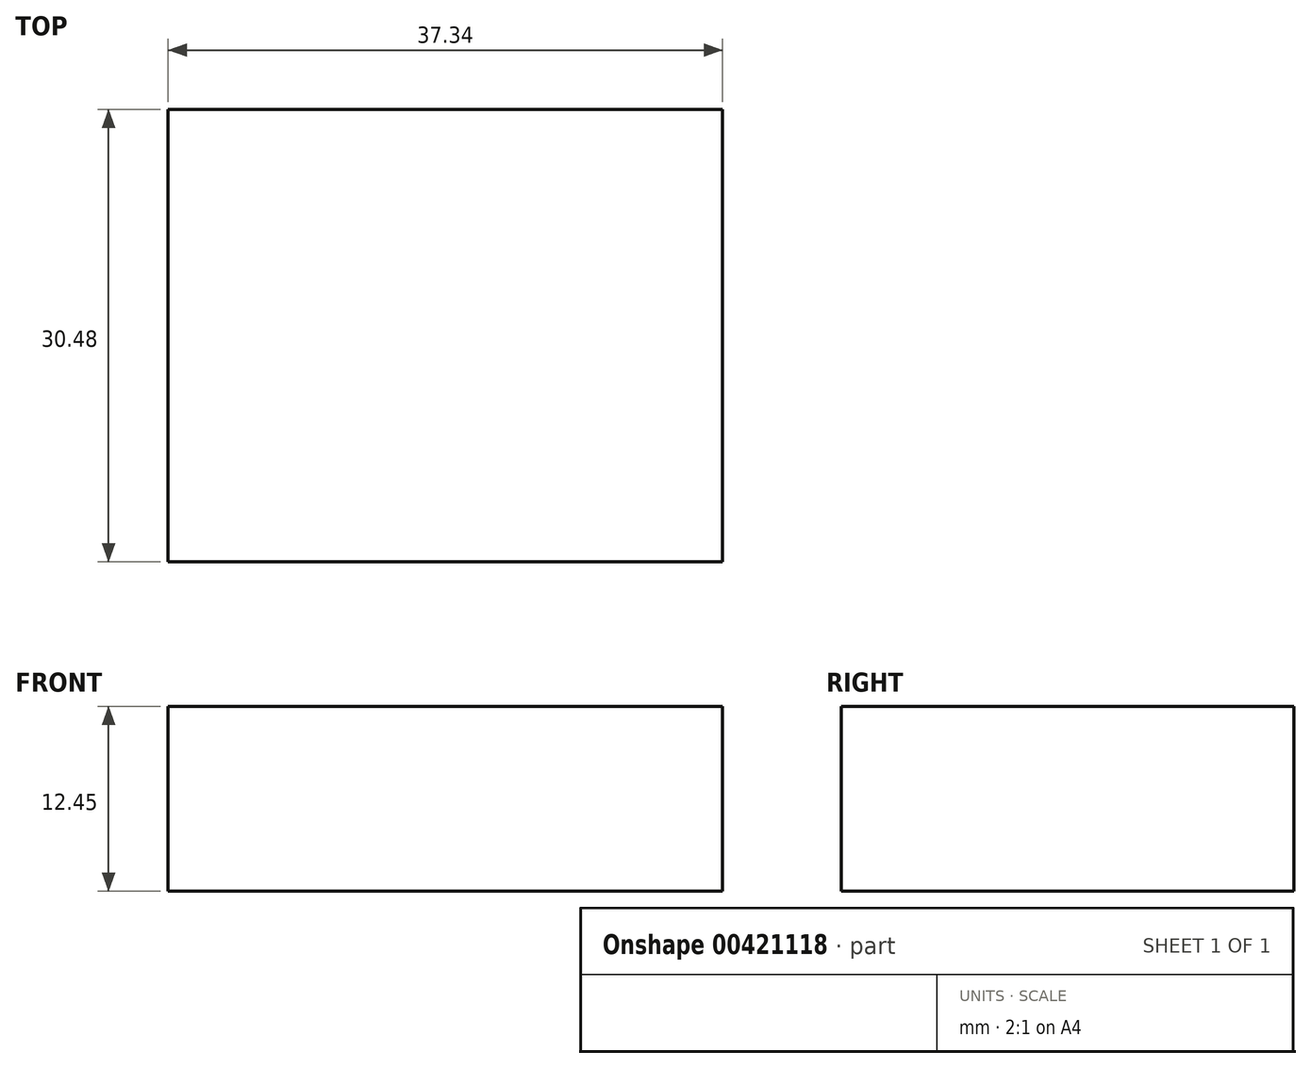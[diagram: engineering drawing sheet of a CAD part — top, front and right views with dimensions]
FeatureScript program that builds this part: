
annotation { "Feature Type Name" : "Feature", "Feature Type Description" : "" }
export const myFeature = defineFeature(function(context is Context, id is Id, definition is map)
    precondition{}
    {
        {
            var Q0;
            Q0=qCreatedBy(makeId("Top.planeOp"),FACE);
            var sketch = newSketch(context, id + "F0", { "sketchPlane" : qUnion([Q0])});
            skLineSegment(sketch, "E0.bottom", {"start": v(0, 0) * mm, "end": v(37.34, 0) * mm});
            skLineSegment(sketch, "E0.top", {"start": v(0, 30.48) * mm, "end": v(37.34, 30.48) * mm});
            skLineSegment(sketch, "E0.left", {"start": v(0, 0) * mm, "end": v(0, 30.48) * mm});
            skLineSegment(sketch, "E0.right", {"start": v(37.34, 0) * mm, "end": v(37.34, 30.48) * mm});
            skSolve(sketch);
        }
        {
            var Q0;
            Q0 = qSketchRegion(id + "F0", true);
            extrude(context, id + "F1", {"entities" : qUnion([Q0]), "depth" : 12.45 * mm});
        }
    });
